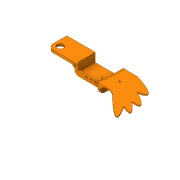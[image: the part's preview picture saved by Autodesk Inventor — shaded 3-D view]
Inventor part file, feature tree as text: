
AUTODESK INVENTOR PART (.ipt)
format: ipt  version: 2016 (Build 200138000, 138)  size: 195,072 bytes
history: native  units: in
note: dims shown in document units (in); Inventor stores cm internally (conversion verified against a paired STEP export)
features: other x3, fillet x1
ambient origin geometry x8: Origin, YZ Plane, XZ Plane, XY Plane, X Axis, Y Axis, Z Axis, Center Point
bodies: Solid1 (feature_tree)
feature tree (4):
  other  "P_ankle02_001.ipt"
  fillet  "Fillet1"  Radius=0.3937in
  other  "Solid1::P_ankle02_001.ipt"
  other  "TaggingFeature1"
